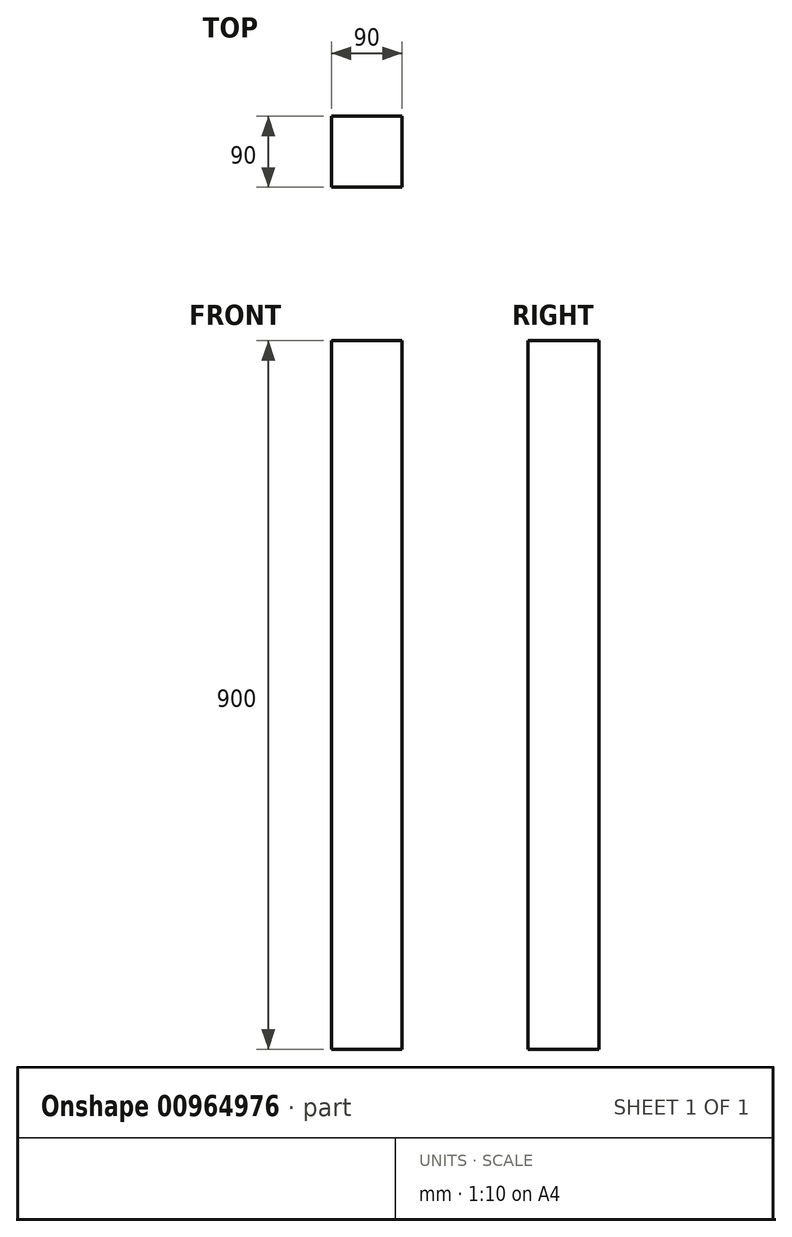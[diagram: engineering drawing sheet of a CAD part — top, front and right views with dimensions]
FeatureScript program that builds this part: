
annotation { "Feature Type Name" : "Feature", "Feature Type Description" : "" }
export const myFeature = defineFeature(function(context is Context, id is Id, definition is map)
    precondition{}
    {
        {
            var Q0;
            Q0=qCreatedBy(makeId("Top.planeOp"),FACE);
            var sketch = newSketch(context, id + "F0", { "sketchPlane" : qUnion([Q0])});
            skLineSegment(sketch, "E0.bottom", {"start": v(39.36, -30.23) * mm, "end": v(-50.64, -30.23) * mm});
            skLineSegment(sketch, "E0.top", {"start": v(39.36, 59.77) * mm, "end": v(-50.64, 59.77) * mm});
            skLineSegment(sketch, "E0.left", {"start": v(39.36, -30.23) * mm, "end": v(39.36, 59.77) * mm});
            skLineSegment(sketch, "E0.right", {"start": v(-50.64, -30.23) * mm, "end": v(-50.64, 59.77) * mm});
            skPoint(sketch, "E0.middle", {"position": v(-5.64, 14.77) * mm});
            skSolve(sketch);
        }
        {
            var Q0;
            Q0=makeQuery(id+"F0.imprint","IMPRINT",FACE,{"disambiguationData":[TD([[makeQuery(id+"F0.imprint","IMPRINT",EDGE,{"derivedFrom":sQuery(id+"F0.wireOp",EDGE,"E0.bottom")}),-1.0]])]});
            extrude(context, id + "F1", {"entities" : qUnion([Q0]), "depth" : 900 * mm, "offsetDistance" : 25 * mm});
        }
    });
